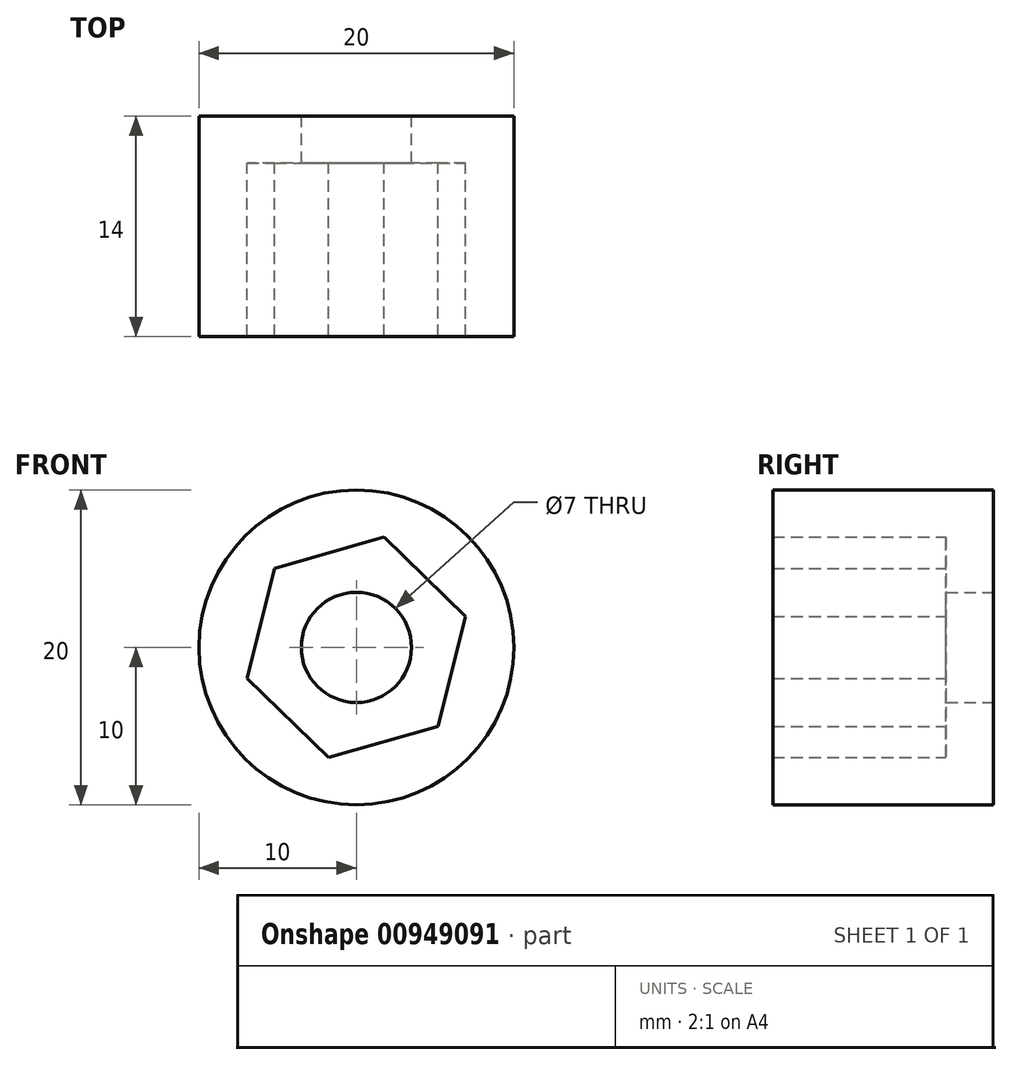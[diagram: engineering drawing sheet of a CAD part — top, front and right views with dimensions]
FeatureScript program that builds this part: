
annotation { "Feature Type Name" : "Feature", "Feature Type Description" : "" }
export const myFeature = defineFeature(function(context is Context, id is Id, definition is map)
    precondition{}
    {
        {
            var Q0;
            Q0=qCreatedBy(makeId("Front.planeOp"),FACE);
            var sketch = newSketch(context, id + "F0", { "sketchPlane" : qUnion([Q0])});
            skCircle(sketch, "E0", {"center": v(0, 0) * mm, "radius": 10 * mm});
            skCircle(sketch, "E1.cCircle", {"center": v(0, 0) * mm, "radius": 6.25 * mm, "construction": true});
            skLineSegment(sketch, "E1.0", {"start": v(1.76, 7) * mm, "end": v(6.94, 1.98) * mm});
            skLineSegment(sketch, "E1.1", {"start": v(6.94, 1.98) * mm, "end": v(5.18, -5.02) * mm});
            skLineSegment(sketch, "E1.2", {"start": v(5.18, -5.02) * mm, "end": v(-1.76, -7) * mm});
            skLineSegment(sketch, "E1.3", {"start": v(-1.76, -7) * mm, "end": v(-6.94, -1.98) * mm});
            skLineSegment(sketch, "E1.4", {"start": v(-6.94, -1.98) * mm, "end": v(-5.18, 5.02) * mm});
            skLineSegment(sketch, "E1.5", {"start": v(-5.18, 5.02) * mm, "end": v(1.76, 7) * mm});
            skPoint(sketch, "E1.0.midPoint", {"position": v(4.35, 4.49) * mm});
            skCircle(sketch, "E2", {"center": v(0, 0) * mm, "radius": 3.5 * mm});
            skSolve(sketch);
        }
        {
            var Q0;
            Q0 = qSketchRegion(id + "F0", true);
            extrude(context, id + "F1", {"entities" : qUnion([Q0]), "depth" : 14 * mm, "offsetDistance" : 25.4 * mm});
        }
        {
            var Q0;
            Q0=makeQuery(id+"F0.imprint","IMPRINT",FACE,{"disambiguationData":[TD([[makeQuery(id+"F0.imprint","IMPRINT",EDGE,{"derivedFrom":sQuery(id+"F0.wireOp",EDGE,"E1.0")}),-1.0]])]});
            extrude(context, id + "F2", {"entities" : qUnion([Q0]), "operationType" : NewBodyOperationType.ADD, "depth" : 3 * mm, "offsetDistance" : 25.4 * mm});
        }
    });
